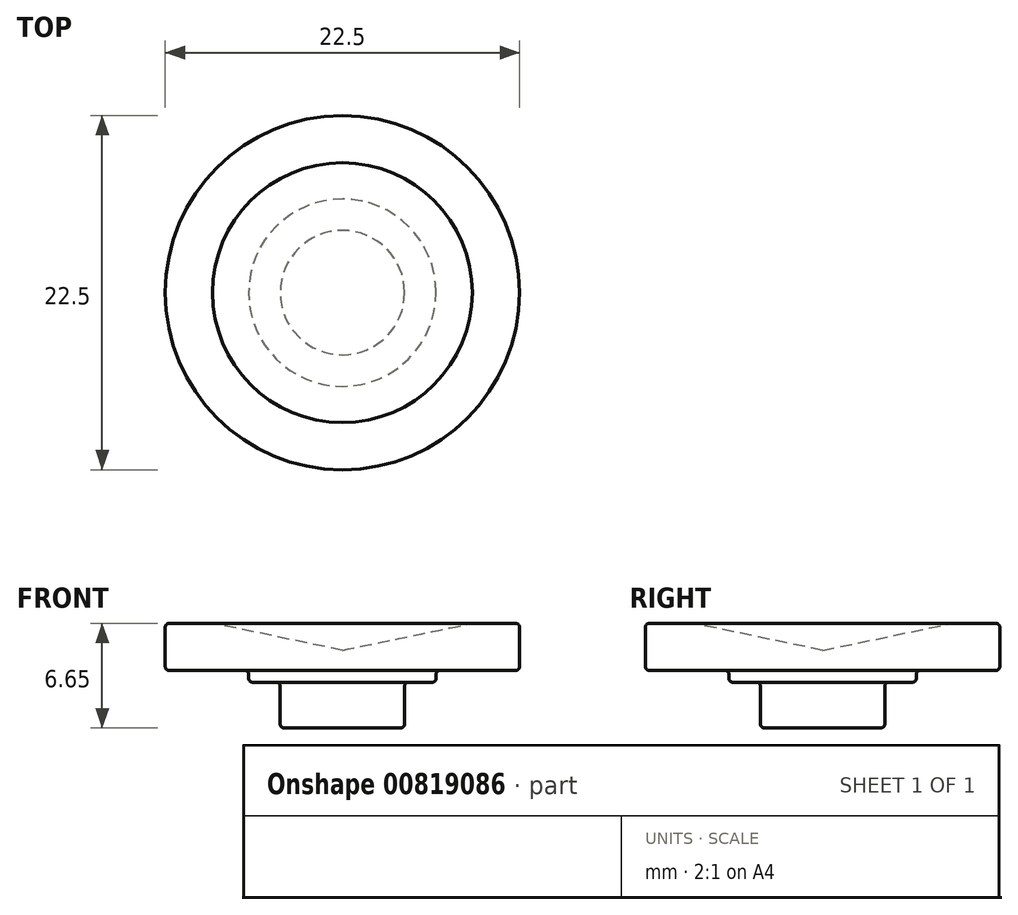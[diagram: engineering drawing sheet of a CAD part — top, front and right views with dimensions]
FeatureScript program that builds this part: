
annotation { "Feature Type Name" : "Feature", "Feature Type Description" : "" }
export const myFeature = defineFeature(function(context is Context, id is Id, definition is map)
    precondition{}
    {
        {
            var Q0;
            Q0=qCreatedBy(makeId("Top.planeOp"),FACE);
            var sketch = newSketch(context, id + "F0", { "sketchPlane" : qUnion([Q0])});
            skCircle(sketch, "E0", {"center": v(0, 0) * mm, "radius": 11.25 * mm});
            skCircle(sketch, "E1", {"center": v(0, 0) * mm, "radius": 8.25 * mm});
            skCircle(sketch, "E2", {"center": v(0, 0) * mm, "radius": 5.95 * mm});
            skCircle(sketch, "E3", {"center": v(0, 0) * mm, "radius": 3.95 * mm});
            skSolve(sketch);
        }
        {
            var Q0;
            Q0=makeQuery(id+"F0.imprint","IMPRINT",FACE,{"disambiguationData":[TD([[makeQuery(id+"F0.imprint","IMPRINT",EDGE,{"derivedFrom":sQuery(id+"F0.wireOp",EDGE,"E0")}),1.0]])]});
            var Q1;
            Q1=makeQuery(id+"F0.imprint","IMPRINT",FACE,{"disambiguationData":[TD([[makeQuery(id+"F0.imprint","IMPRINT",EDGE,{"derivedFrom":sQuery(id+"F0.wireOp",EDGE,"E1")}),1.0]])]});
            var Q2;
            Q2=makeQuery(id+"F0.imprint","IMPRINT",FACE,{"disambiguationData":[TD([[makeQuery(id+"F0.imprint","IMPRINT",EDGE,{"derivedFrom":sQuery(id+"F0.wireOp",EDGE,"E2")}),1.0]])]});
            var Q3;
            Q3=makeQuery(id+"F0.imprint","IMPRINT",FACE,{"disambiguationData":[TD([[makeQuery(id+"F0.imprint","IMPRINT",EDGE,{"derivedFrom":sQuery(id+"F0.wireOp",EDGE,"E3")}),1.0]])]});
            extrude(context, id + "F1", {"entities" : qUnion([Q0, Q1, Q2, Q3]), "depth" : 3 * mm, "offsetDistance" : 25 * mm});
        }
        {
            var Q0;
            Q0=makeQuery(id+"F0.imprint","IMPRINT",FACE,{"disambiguationData":[TD([[makeQuery(id+"F0.imprint","IMPRINT",EDGE,{"derivedFrom":sQuery(id+"F0.wireOp",EDGE,"E2")}),1.0]])]});
            var Q1;
            Q1=makeQuery(id+"F0.imprint","IMPRINT",FACE,{"disambiguationData":[TD([[makeQuery(id+"F0.imprint","IMPRINT",EDGE,{"derivedFrom":sQuery(id+"F0.wireOp",EDGE,"E3")}),1.0]])]});
            extrude(context, id + "F2", {"entities" : qUnion([Q0, Q1]), "operationType" : NewBodyOperationType.ADD, "oppositeDirection" : true, "depth" : .75 * mm, "offsetDistance" : 25 * mm});
        }
        {
            var Q0;
            Q0=makeQuery(id+"F0.imprint","IMPRINT",FACE,{"disambiguationData":[TD([[makeQuery(id+"F0.imprint","IMPRINT",EDGE,{"derivedFrom":sQuery(id+"F0.wireOp",EDGE,"E3")}),1.0]])]});
            extrude(context, id + "F3", {"entities" : qUnion([Q0]), "operationType" : NewBodyOperationType.ADD, "oppositeDirection" : true, "depth" : 3.65 * mm, "offsetDistance" : 25 * mm});
        }
        {
            var Q0;
            Q0=qCreatedBy(makeId("Front.planeOp"),FACE);
            var sketch = newSketch(context, id + "F4", { "sketchPlane" : qUnion([Q0])});
            skLineSegment(sketch, "E4", {"start": v(0, 1.28) * mm, "end": v(8.25, 3) * mm});
            skLineSegment(sketch, "E5", {"start": v(0, 1.28) * mm, "end": v(0, 3) * mm});
            skLineSegment(sketch, "E6", {"start": v(8.25, 3) * mm, "end": v(0, 3) * mm});
            skSolve(sketch);
        }
        {
            var Q0;
            Q0=makeQuery(id+"F4.imprint","IMPRINT",FACE,{"disambiguationData":[TD([[makeQuery(id+"F4.imprint","IMPRINT",EDGE,{"derivedFrom":sQuery(id+"F4.wireOp",EDGE,"E4")}),1.0]])]});
            var Q1;
            Q1=sQuery(id+"F4.wireOp",EDGE,"E5");
            revolve(context, id + "F5", {"operationType" : NewBodyOperationType.REMOVE, "surfaceOperationType" : NewSurfaceOperationType.NEW, "entities" : qUnion([Q0]), "axis" : qUnion([Q1]), "revolveType" : RevolveType.FULL, "oppositeDirection" : true});
        }
        {
            var Q0;
            Q0=makeQuery(id+"F5.boolean.opBoolean","COPY",EDGE,{"derivedFrom":makeQuery(id+"F5.opRevolve","SWEPT_EDGE",EDGE,{"disambiguationData":[OSD([sQuery(id+"F4.wireOp",EDGE,"E4"),sQuery(id+"F4.wireOp",EDGE,"E6")])]})});
            var Q1;
            Q1=makeQuery(id+"F1.opExtrude","CAP_EDGE",EDGE,{"disambiguationData":[OSD([sQuery(id+"F0.wireOp",EDGE,"E0")])],"isStart":false});
            var Q2;
            Q2=makeQuery(id+"F1.opExtrude","CAP_EDGE",EDGE,{"disambiguationData":[OSD([sQuery(id+"F0.wireOp",EDGE,"E0")])],"isStart":true});
            var Q3;
            Q3=makeQuery(id+"F3.opExtrude","CAP_EDGE",EDGE,{"disambiguationData":[OSD([sQuery(id+"F0.wireOp",EDGE,"E3")])],"isStart":false});
            var Q4;
            Q4=makeQuery(id+"F3.boolean.opBoolean","INTERSECT",EDGE,{"derivedFrom":[makeQuery(id+"F2.opExtrude","CAP_FACE",FACE,{"disambiguationData":[OSD([sQuery(id+"F0.wireOp",EDGE,"E2")])],"isStart":false}),makeQuery(id+"F3.opExtrude","SWEPT_FACE",FACE,{"disambiguationData":[OSD([sQuery(id+"F0.wireOp",EDGE,"E3")])]})]});
            var Q5;
            Q5=makeQuery(id+"F2.opExtrude","CAP_EDGE",EDGE,{"disambiguationData":[OSD([sQuery(id+"F0.wireOp",EDGE,"E2")])],"isStart":false});
            var Q6;
            Q6=makeQuery(id+"F2.opExtrude","SWEPT_FACE",FACE,{"disambiguationData":[OSD([sQuery(id+"F0.wireOp",EDGE,"E2")])]});
            fillet(context, id + "F6", {"entities" : qUnion([Q0, Q1, Q2, Q3, Q4, Q5, Q6]), "radius" : .25 * mm, "tangentPropagation" : true, "allowEdgeOverflow" : false});
        }
    });
